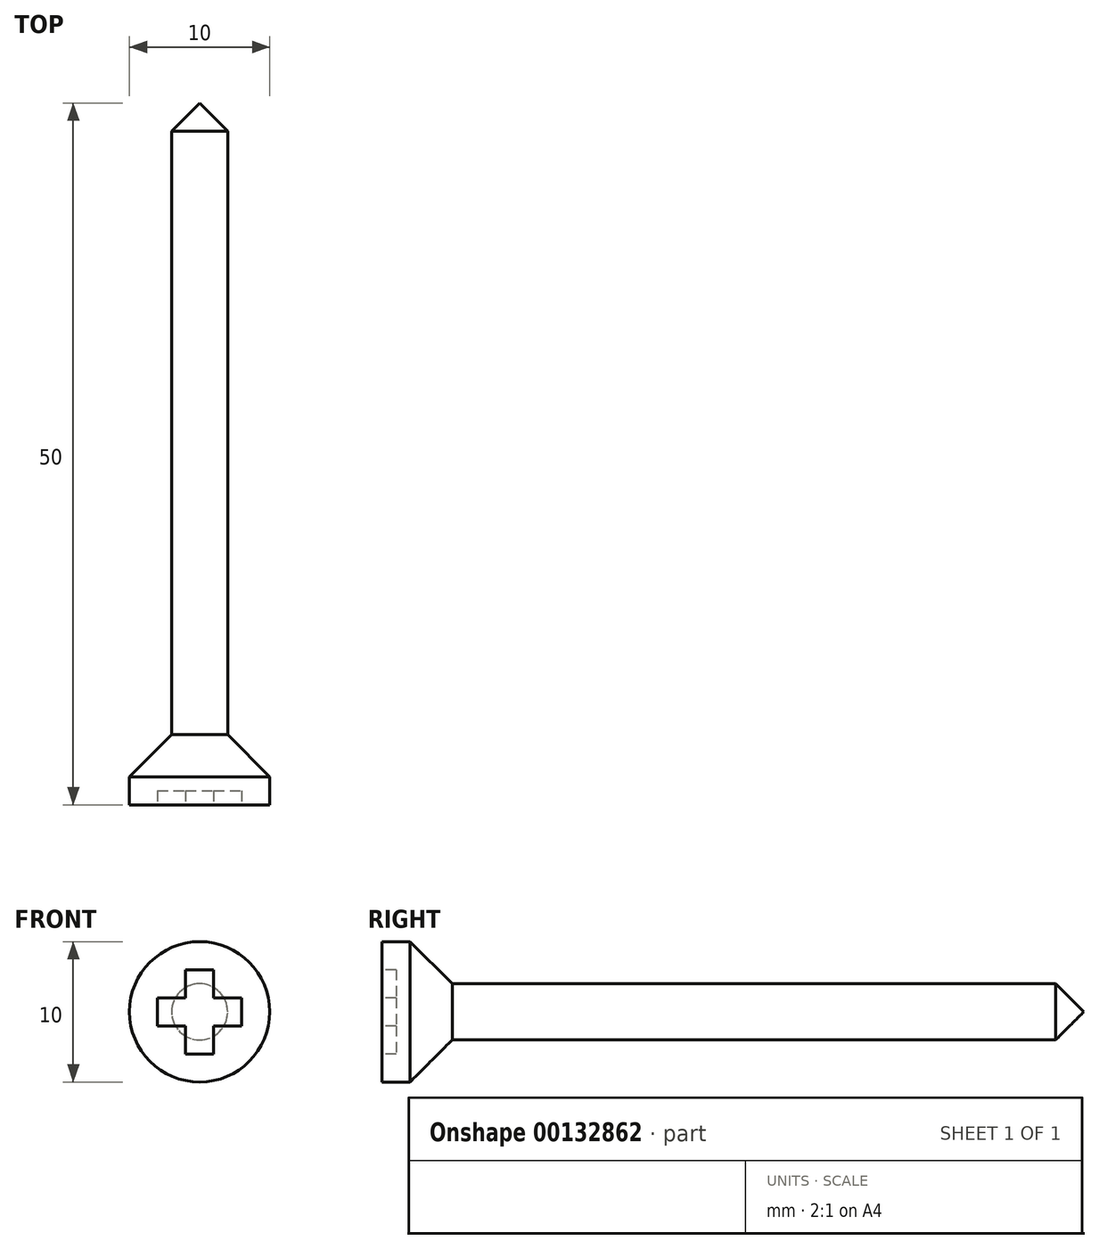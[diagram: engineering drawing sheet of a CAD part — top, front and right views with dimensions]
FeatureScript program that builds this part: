
annotation { "Feature Type Name" : "Feature", "Feature Type Description" : "" }
export const myFeature = defineFeature(function(context is Context, id is Id, definition is map)
    precondition{}
    {
        {
            var Q0;
            Q0=qCreatedBy(makeId("Front.planeOp"),FACE);
            var sketch = newSketch(context, id + "F0", { "sketchPlane" : qUnion([Q0])});
            skCircle(sketch, "E0", {"center": v(0, 0) * mm, "radius": 5 * mm});
            skSolve(sketch);
        }
        {
            var Q0;
            Q0 = qSketchRegion(id + "F0", true);
            extrude(context, id + "F1", {"entities" : qUnion([Q0]), "depth" : 5 * mm, "offsetDistance" : 25 * mm});
        }
        {
            var Q0;
            Q0=makeQuery(id+"F1.opExtrude","CAP_EDGE",EDGE,{"disambiguationData":[OSD([sQuery(id+"F0.wireOp",EDGE,"E0")])],"isStart":true});
            chamfer(context, id + "F2", {"entities" : qUnion([Q0]), "width" : 3 * mm, "tangentPropagation" : true});
        }
        {
            var Q0;
            Q0=makeQuery(id+"F1.opExtrude","CAP_FACE",FACE,{"disambiguationData":[OSD([sQuery(id+"F0.wireOp",EDGE,"E0")])],"isStart":true});
            var sketch = newSketch(context, id + "F3", { "sketchPlane" : qUnion([Q0])});
            skCircle(sketch, "E1", {"center": v(0, 0) * mm, "radius": 2 * mm});
            skSolve(sketch);
        }
        {
            var Q0;
            Q0 = qSketchRegion(id + "F3", true);
            extrude(context, id + "F4", {"entities" : qUnion([Q0]), "operationType" : NewBodyOperationType.ADD, "depth" : 45 * mm, "offsetDistance" : 25 * mm});
        }
        {
            var Q0;
            Q0=makeQuery(id+"F4.opExtrude","CAP_EDGE",EDGE,{"disambiguationData":[OSD([sQuery(id+"F3.wireOp",EDGE,"E1")])],"isStart":false});
            chamfer(context, id + "F5", {"entities" : qUnion([Q0]), "width" : 2 * mm, "tangentPropagation" : true});
        }
        {
            var Q0;
            Q0=makeQuery(id+"F1.opExtrude","CAP_FACE",FACE,{"disambiguationData":[OSD([sQuery(id+"F0.wireOp",EDGE,"E0")])],"isStart":false});
            var sketch = newSketch(context, id + "F6", { "sketchPlane" : qUnion([Q0])});
            skLineSegment(sketch, "E2.bottom", {"start": v(-1, 3) * mm, "end": v(1, 3) * mm});
            skLineSegment(sketch, "E2.top", {"start": v(-1, -3) * mm, "end": v(1, -3) * mm});
            skLineSegment(sketch, "E2.left", {"start": v(-1, 3) * mm, "end": v(-1, 1) * mm});
            skLineSegment(sketch, "E2.right", {"start": v(1, 3) * mm, "end": v(1, 1) * mm});
            skLineSegment(sketch, "E3.bottom", {"start": v(-3, 1) * mm, "end": v(-1, 1) * mm});
            skLineSegment(sketch, "E3.left", {"start": v(-3, 1) * mm, "end": v(-3, -1) * mm});
            skLineSegment(sketch, "E3.right", {"start": v(3, 1) * mm, "end": v(3, -1) * mm});
            skLineSegment(sketch, "E4.trimOffspring", {"start": v(1, 1) * mm, "end": v(3, 1) * mm});
            skLineSegment(sketch, "E5.trimOffspring", {"start": v(1, -1) * mm, "end": v(1, -3) * mm});
            skLineSegment(sketch, "E6.trimOffspring", {"start": v(-1, -1) * mm, "end": v(-1, -3) * mm});
            skLineSegment(sketch, "E7.trimOffspring", {"start": v(1, -1) * mm, "end": v(3, -1) * mm});
            skLineSegment(sketch, "E8", {"start": v(-3, -1) * mm, "end": v(-1, -1) * mm});
            skSolve(sketch);
        }
        {
            var Q0;
            Q0 = qSketchRegion(id + "F6", true);
            extrude(context, id + "F7", {"entities" : qUnion([Q0]), "operationType" : NewBodyOperationType.REMOVE, "oppositeDirection" : true, "depth" : 1 * mm, "offsetDistance" : 25 * mm});
        }
    });
